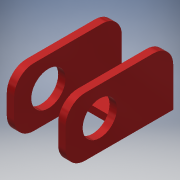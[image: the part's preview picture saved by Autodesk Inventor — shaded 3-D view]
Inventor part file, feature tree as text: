
AUTODESK INVENTOR PART (.ipt)
format: ipt  version: 2017 SP1 (Build 210196100, 196)  size: 162,304 bytes
history: native  units: in
note: dims shown in document units (in); Inventor stores cm internally (conversion verified against a paired STEP export)
features: extrude x3, sketch x3, fillet x1
ambient origin geometry x8: Origin, YZ Plane, XZ Plane, XY Plane, X Axis, Y Axis, Z Axis, Center Point
bodies: Solid1 (feature_tree)
feature tree (7):
  extrude  "Extrusion1"  Depth=1.5in
  extrude  "Extrusion2"  Depth=2.75in TaperAngle=0.0deg
  extrude  "Extrusion3"  Depth=0.75in
  fillet  "Fillet1"  Radius=0.75in
  sketch  "Sketch1"  dims[d0=0.1875in d2=1.5in]
  sketch  "Sketch2"  dims[d3=1.5in d4=2.75in d5=0.0in]
  sketch  "Sketch3"  dims[d6=0.2in d7=0.75in d8=0.75in d10=0.5625in d11=2.5in d12=0.0in d13=0.875in d14=0.75in d15=1.125in d16=1.3125in d17=2.5in d18=0.0in d19=0.5in d21=0.1875in d22=0.1875in]
